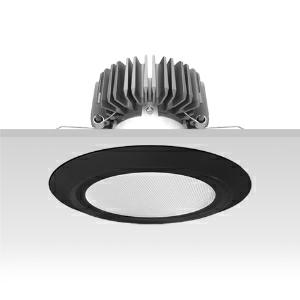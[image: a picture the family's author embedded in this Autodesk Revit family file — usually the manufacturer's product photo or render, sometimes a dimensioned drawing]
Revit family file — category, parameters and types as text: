
# Revit family: 3f_filippi_-_3f_reno_bianco_ampio_3f_filippi_-_30629_a01038_-_3f_reno_200_wh_3000-840_wide___vs_bk_1715
name_source: partatom
category: Lighting Fixtures
units: mm (PartAtom-declared; Revit-internal decimal feet)

## family parameters
Cut with Voids When Loaded = No
Host = Face
Light Source = No
Part Type = Normal
Room Calculation Point = No
Round Connector Dimension = Use Diameter
Shared = No

## types (1)
- 3F Filippi - 3F Reno Bianco Ampio (1 x LED, 2312 lm, 28 W, 4000 K)
    Apparent Load = 28 VA
    Approval mark = CE
    CIE Flux Codes = 75 94 99 100 100
    Color Rendering = 80
    Color Temperature = 4000 K
    Control Gear = Electronic ballast
    Default Elevation = 1800 mm
    Description = ILLUMINOTECHNICAL
Luminous efficiency 100% (DLOR 100%, ULOR 0%).
Initial luminous flux of the luminaire 2312 lm.
Direct symmetric wide distribution.
Installation Interdistance Transv.D = 1.16 x hu - Long.D = 1.14 x hu.
Tabular UGR (CIE 117 - 4H-8H; S=0.25H; 70/50/20): RUG 21.5 - 21.4.
Beam angle: 74° - 74°.
Luminous efficacy 83 lm/W.
Lifetime (L90/B10): 30000 h. (tq+25°C)
Lifetime (L85/B10): 50000 h. (tq+25°C)
Lifetime (L70/B10): 80000 h. (tq+25°C)
Sudden decreased luminous flux after 50000 hours: 0% (C0).
Photobiological safety in compliance with IEC/TR 62778: RG0 risk exempt, (IEC 62471).
In compliance with IEC/EN 62722-2-1 - IEC/EN 62717 standards.

SOURCE
Compact LED module 3000/840.
Energy efficiency class (UE 2019/2020 - UE 2019/2015): D.
CIE 13.3 Colour rendering index: CRI >80 (R9 <50%).
IES TM-30 Fidelity Index: Rf = 84 Rg = 95.
CCT nominal colour temperature 4000 K.
Colour initial tolerance (MacAdam): SDCM 3.
Zhaga Book 3 compliant.

MECHANICAL
Passive heat dissipator in die-casting aluminium, oversized, for optimum thermal management of the LED module.
Parabolic element with graduated/concentric rings in white polycarbonate.
Transparent external lens with glossy and satin differentiated surfaces, with a cooling and anti-insect system in methacrylate (PMMA).
Fastening spring clips in stainless steel.
Dimensions: diameter 226 mm, height 146 mm. Weight 1.76 kg.
IP44 protection degree for exposed part, IP20 for recessed part.
Mechanical strength to impacts IK06 (1 joule).
Glow-wire test resistance 650°C.

ELECTRICAL
Wiring on a separate unit.
Halogen Free electronic wiring 230V-50/60Hz, power factor 0.95, THD <25%, constant output current, SELV, class II, 1 driver.
Power of the luminaire 28 W.
ENEC - CE.
SAFE FLICKER: PstLM=<1 and SVM=<0.4 (IEC TR 61547-1 and IEC TR 63158), to ensure a more comfortable and safe light.
Luminaire compliant with EN 60598-2-22 for power supply from a centralised emergency system CPSS (Central Power Supply System), not incorporated in the luminaire - high risk areas excluded. The default power and flux are 100% in AC and 100% in DC.
Ambient temperature from 0°C to +25°C.
Temperature class T6 max 85°C.
Relative humidity UR: <85%.

INSTALLATION
Pull-up recessed fitting.
False ceiling carving: 200 mm.
All accessories dedicated to this product are available on the Catalog and on our website www.3F-Filippi.com.

ACCESSORIES
A01038 - Anti-glare microprismatic VS moulded glass, tempered, not flammable, locked and in line with the trim, in black polycarbonate.

APPLICATIONS
Environments: architectural, commercial, exhibition areas, transit areas, corridors, shops, display windows, service areas.
In false ceilings with narrow voids.

WARNING
Luminaire designed for disposal/recycling at end-of-life.
Replaceable (LED only) light source by a professional. Replaceable control gear by a professional.
    Height = 0 mm  [stored 0 ft]
    Lamp = 1 x LED
    Lamp Light Flux = 2312 lm
    Lamp Power = 28 W
    Lamp count = 1
    Length = 226 mm
    Lifetime = 50000 h
    Luminous efficacy = 83 lm/W
    Manufacturer = 3F Filippi
    ModVariant = No
    Model = 3F Filippi - 30629+A01038 - 3F Reno 200 WH 3000-840 WIDE + VS BK
    Mounting Place = Ceiling
    Mounting Type = Recessed
    Number of Poles = 1
    OnlyDefault = Yes
    Power Factor = 1
    Product Name = 3F Filippi - 3F Reno Bianco Ampio
    Product group = recessed luminaire
    ProductGroupID = 4
    Protection Class = Protection class II
    Protection Degree = IP 20
    RLX_Detail_Level = 1
    RLX_Emergency_Light_Flux = 0 lm
    RLX_Emergency_Type = 0
    RLX_Emergency_Type_DB = No
    RlxData = <blob elided: 96393 chars, md5=3629b5ce>
    Socket = socket
    Standby Power = 0 W
    System Light Flux = 2312 lm
    System Power = 28 W
    Type Comments = Product without accessories
    Type Image = 3ffilippi_3f_reno_200_bk_vs_smp.jpg
    URL = http://relux.com
    VarID = ---
    Voltage = 0 V
    Weight = 0.00 kg
    Width = 0 mm  [stored 0 ft]

note: [stored X ft] marks values corroborated as IEEE doubles in the binary element streams (Revit-internal decimal feet)

## geometry (parser evidence)
native form markers: Blend x4, Sweep x9
no freeform markers — native parametric forms only
